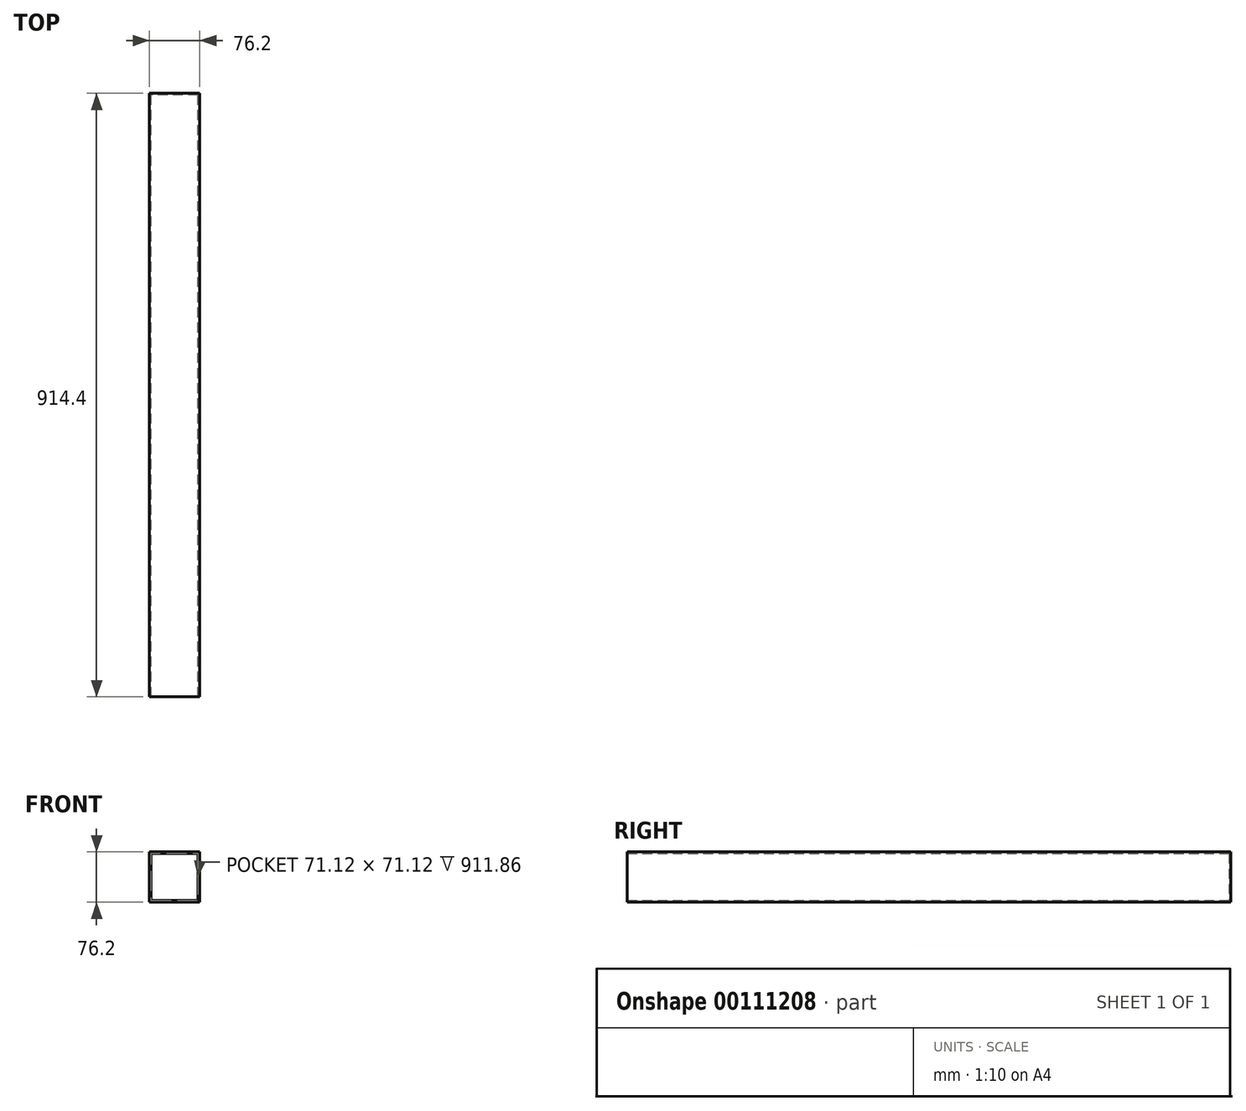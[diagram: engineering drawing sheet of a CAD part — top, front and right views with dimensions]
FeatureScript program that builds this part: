
annotation { "Feature Type Name" : "Feature", "Feature Type Description" : "" }
export const myFeature = defineFeature(function(context is Context, id is Id, definition is map)
    precondition{}
    {
        {
            var Q0;
            Q0=qCreatedBy(makeId("Front.planeOp"),FACE);
            var sketch = newSketch(context, id + "F0", { "sketchPlane" : qUnion([Q0])});
            skLineSegment(sketch, "E0.bottom", {"start": v(38.1, 38.1) * mm, "end": v(-38.1, 38.1) * mm});
            skLineSegment(sketch, "E0.top", {"start": v(38.1, -38.1) * mm, "end": v(-38.1, -38.1) * mm});
            skLineSegment(sketch, "E0.left", {"start": v(38.1, 38.1) * mm, "end": v(38.1, -38.1) * mm});
            skLineSegment(sketch, "E0.right", {"start": v(-38.1, 38.1) * mm, "end": v(-38.1, -38.1) * mm});
            skPoint(sketch, "E0.middle", {"position": v(0, 0) * mm});
            skSolve(sketch);
        }
        {
            var Q0;
            Q0=makeQuery(id+"F0.imprint","IMPRINT",FACE,{"disambiguationData":[TD([[makeQuery(id+"F0.imprint","IMPRINT",EDGE,{"derivedFrom":sQuery(id+"F0.wireOp",EDGE,"E0.bottom")}),1.0]])]});
            extrude(context, id + "F1", {"entities" : qUnion([Q0]), "depth" : 914.4 * mm});
        }
        {
            var Q0;
            Q0=makeQuery(id+"F1.opExtrude","CAP_FACE",FACE,{"disambiguationData":[OSD([sQuery(id+"F0.wireOp",EDGE,"E0.bottom"),sQuery(id+"F0.wireOp",EDGE,"E0.top"),sQuery(id+"F0.wireOp",EDGE,"E0.left"),sQuery(id+"F0.wireOp",EDGE,"E0.right")])],"isStart":false});
            shell(context, id + "F2", {"entities" : qUnion([Q0]), "thickness" : 2.54 * mm});
        }
    });
